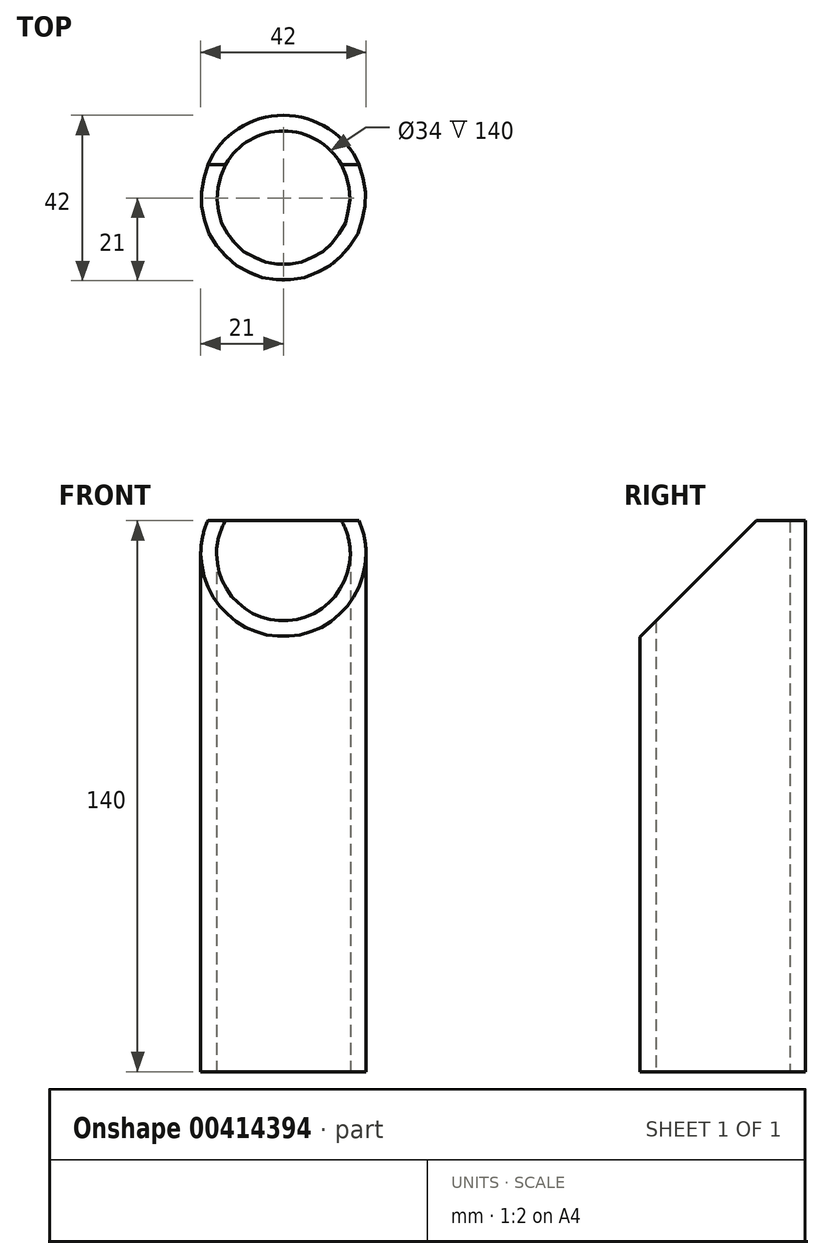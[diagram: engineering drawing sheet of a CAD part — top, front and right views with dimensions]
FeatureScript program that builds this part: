
annotation { "Feature Type Name" : "Feature", "Feature Type Description" : "" }
export const myFeature = defineFeature(function(context is Context, id is Id, definition is map)
    precondition{}
    {
        {
            var Q0;
            Q0=qCreatedBy(makeId("Top.planeOp"),FACE);
            var sketch = newSketch(context, id + "F0", { "sketchPlane" : qUnion([Q0])});
            skCircle(sketch, "E0", {"center": v(0, 0) * mm, "radius": 17 * mm});
            skCircle(sketch, "E1.0", {"center": v(0, 0) * mm, "radius": 21 * mm});
            skSolve(sketch);
        }
        {
            var Q0;
            Q0 = qSketchRegion(id + "F0", true);
            extrude(context, id + "F1", {"entities" : qUnion([Q0]), "endBound" : BoundingType.SYMMETRIC, "offsetDistance" : 25 * mm, "depth" : 140 * mm});
        }
        {
            var Q0;
            Q0=qCreatedBy(makeId("Right.planeOp"),FACE);
            var sketch = newSketch(context, id + "F2", { "sketchPlane" : qUnion([Q0])});
            skLineSegment(sketch, "E2", {"start": v(8.5, 70) * mm, "end": v(-21, 40.5) * mm});
            skLineSegment(sketch, "E3", {"start": v(8.5, 70) * mm, "end": v(21, 70) * mm});
            skLineSegment(sketch, "E4", {"start": v(-21, 40.5) * mm, "end": v(-21, 80) * mm});
            skLineSegment(sketch, "E5", {"start": v(-21, 80) * mm, "end": v(21, 80) * mm});
            skLineSegment(sketch, "E6", {"start": v(21, 80) * mm, "end": v(21, 70) * mm});
            skPoint(sketch, "E7", {"position": v(0, 80) * mm});
            skSolve(sketch);
        }
        {
            var Q0;
            Q0 = qSketchRegion(id + "F2", true);
            extrude(context, id + "F3", {"entities" : qUnion([Q0]), "operationType" : NewBodyOperationType.REMOVE, "endBound" : BoundingType.SYMMETRIC, "oppositeDirection" : true, "depth" : 42 * mm});
        }
    });
